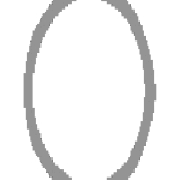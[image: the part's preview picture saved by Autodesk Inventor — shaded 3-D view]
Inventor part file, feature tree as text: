
AUTODESK INVENTOR PART (.ipt)
format: ipt  version: 2021 (Build 250183000, 183)  size: 142,336 bytes
history: native  units: in
note: dims shown in document units (in); Inventor stores cm internally (conversion verified against a paired STEP export)
features: plane x7, sketch x5, other x4, extrude x2, boolean_combine x2
ambient origin geometry x8: Origin, YZ Plane, XZ Plane, XY Plane, X Axis, Y Axis, Z Axis, Center Point
bodies: Solid1 (feature_tree), Body (feature_tree), Solid2 (feature_tree), Solid3 (feature_tree)
feature tree (20):
  other  "Driven Length"
  other  "Frame Generator"
  other  "Start Plane"
  other  "End Plane"
  plane  "Work Plane4"
  plane  "Work Plane5"
  plane  "Work Plane6"
  extrude  "Extrusion3"  Depth=0.065in
  boolean_combine  "Combine1"
  plane  "Work Plane7"
  plane  "Work Plane8"
  plane  "Work Plane9"
  extrude  "Extrusion4"  TaperAngle=0.0deg  [1 undecoded]
  boolean_combine  "Combine2"
  sketch  "Sketch"  dims[d8=90.0deg d9=12.431in d10=0.12in d11=0.0in d12=0.12in d13=0.0in]
  sketch  "Sketch2"  dims[d0=1.0in d1=0.065in]
  plane  "Work Plane3"
  sketch  "Sketch3"  dims[d2=12.431in d4=-0.0in]
  sketch  "Sketch4"  dims[d5=12.431in]
  sketch  "Sketch5"  dims[d6=0.12in d7=0.0in]
note: 1 required parameter value undecoded (feature->parameter linkage not recoverable at this tier; creation-order binding heuristic only, values carry confidence <= 0.55)
